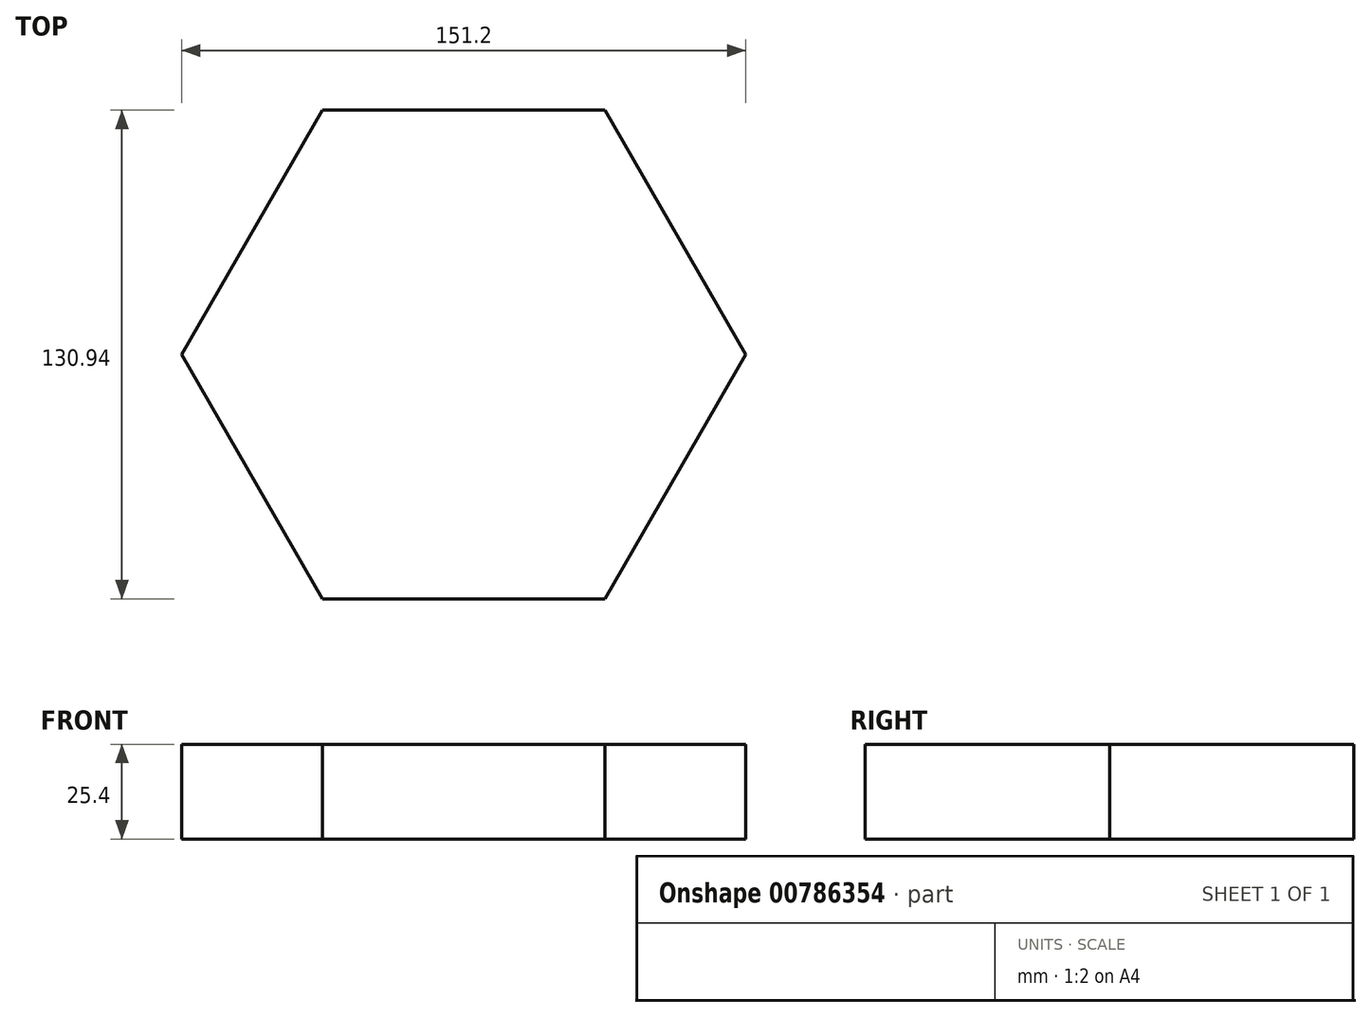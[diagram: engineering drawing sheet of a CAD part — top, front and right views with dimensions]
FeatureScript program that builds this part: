
annotation { "Feature Type Name" : "Feature", "Feature Type Description" : "" }
export const myFeature = defineFeature(function(context is Context, id is Id, definition is map)
    precondition{}
    {
        {
            var Q0;
            Q0=qCreatedBy(makeId("Top.planeOp"),FACE);
            var sketch = newSketch(context, id + "F0", { "sketchPlane" : qUnion([Q0])});
            skCircle(sketch, "E0.cCircle", {"center": v(0, 0) * mm, "radius": 65.47 * mm, "construction": true});
            skLineSegment(sketch, "E0.0", {"start": v(37.8, 65.47) * mm, "end": v(75.6, 0) * mm});
            skLineSegment(sketch, "E0.1", {"start": v(75.6, 0) * mm, "end": v(37.8, -65.47) * mm});
            skLineSegment(sketch, "E0.2", {"start": v(37.8, -65.47) * mm, "end": v(-37.8, -65.47) * mm});
            skLineSegment(sketch, "E0.3", {"start": v(-37.8, -65.47) * mm, "end": v(-75.6, 0) * mm});
            skLineSegment(sketch, "E0.4", {"start": v(-75.6, 0) * mm, "end": v(-37.8, 65.47) * mm});
            skLineSegment(sketch, "E0.5", {"start": v(-37.8, 65.47) * mm, "end": v(37.8, 65.47) * mm});
            skPoint(sketch, "E0.0.midPoint", {"position": v(56.7, 32.74) * mm});
            skSolve(sketch);
        }
        {
            var Q0;
            Q0=makeQuery(id+"F0.imprint","IMPRINT",FACE,{"disambiguationData":[TD([[makeQuery(id+"F0.imprint","IMPRINT",EDGE,{"derivedFrom":sQuery(id+"F0.wireOp",EDGE,"E0.0")}),-1.0]])]});
            extrude(context, id + "F1", {"entities" : qUnion([Q0]), "depth" : 25.4 * mm, "offsetDistance" : 25.4 * mm});
        }
    });
